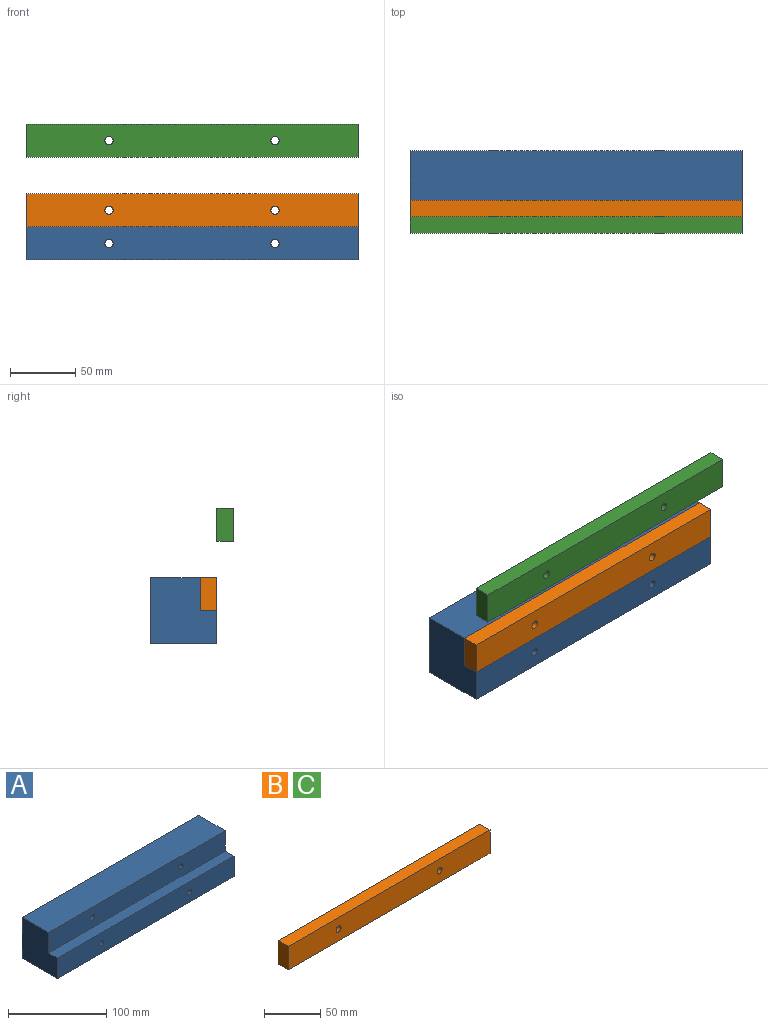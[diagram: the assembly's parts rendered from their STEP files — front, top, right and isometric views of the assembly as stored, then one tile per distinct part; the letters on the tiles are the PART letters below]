
ASSEMBLY  parts=3 mates=2
PART A: 12 faces, bbox 254x50.8x50.8 mm
  f0: plane 254x50.8mm, normal (0,0,-1), area 12903.2mm2, adj f1,f5,f6,f7
  f1: plane 254x50.8mm, normal (0,1,0), area 12776.5mm2, adj f0,f2,f6,f7,f8,f9,f10,f11
  f2: plane 254x38.1mm, normal (0,0,1), area 9677.4mm2, adj f1,f3,f6,f7
  f3: plane 254x25.4mm, normal (0,-1,0), area 6388.3mm2, adj f2,f4,f6,f7,f8,f10
  f4: plane 254x12.7mm, normal (0,0,1), area 3225.8mm2, adj f3,f5,f6,f7
  f5: plane 254x25.4mm, normal (0,-1,0), area 6388.3mm2, adj f0,f4,f6,f7,f9,f11
  f6: plane 50.8x50.8mm, normal (1,0,0), area 2258.1mm2, adj f0,f1,f2,f3,f4,f5
  f7: plane 50.8x50.8mm, normal (-1,0,0), area 2258.1mm2, adj f0,f1,f2,f3,f4,f5
  f8: cylinder r=3.17mm len=38.1mm, axis (0,-1,0), area 760.1mm2, adj f1,f3
  f9: cylinder r=3.17mm len=50.8mm, axis (0,-1,0), area 1013.4mm2, adj f1,f5
  f10: cylinder r=3.17mm len=38.1mm, axis (0,-1,0), area 760.1mm2, adj f1,f3
  f11: cylinder r=3.17mm len=50.8mm, axis (0,-1,0), area 1013.4mm2, adj f1,f5
PART B: 8 faces, bbox 254x12.7x25.4 mm
  f0: plane 254x12.7mm, normal (0,0,1), area 3225.8mm2, adj f1,f3,f4,f5
  f1: plane 254x25.4mm, normal (0,-1,0), area 6388.3mm2, adj f0,f2,f4,f5,f6,f7
  f2: plane 254x12.7mm, normal (0,0,-1), area 3225.8mm2, adj f1,f3,f4,f5
  f3: plane 254x25.4mm, normal (0,1,0), area 6388.3mm2, adj f0,f2,f4,f5,f6,f7
  f4: plane 25.4x12.7mm, normal (1,0,0), area 322.6mm2, adj f0,f1,f2,f3
  f5: plane 25.4x12.7mm, normal (-1,0,0), area 322.6mm2, adj f0,f1,f2,f3
  f6: cylinder r=3.17mm len=12.7mm, axis (0,-1,0), area 253.4mm2, adj f1,f3
  f7: cylinder r=3.17mm len=12.7mm, axis (0,-1,0), area 253.4mm2, adj f1,f3
PART C: same geometry as B
PLACE A at identity fixed
PLACE B t=(0,0,25.4)mm
PLACE C t=(0,-12.7,78.62)mm
MATE planar B.f3 <-> A.f3  axis (0,1,0) through (0,12.7,38.1)mm
MATE planar C.f3 <-> B.f1  axis (0,1,0) through (0,0,91.32)mm
